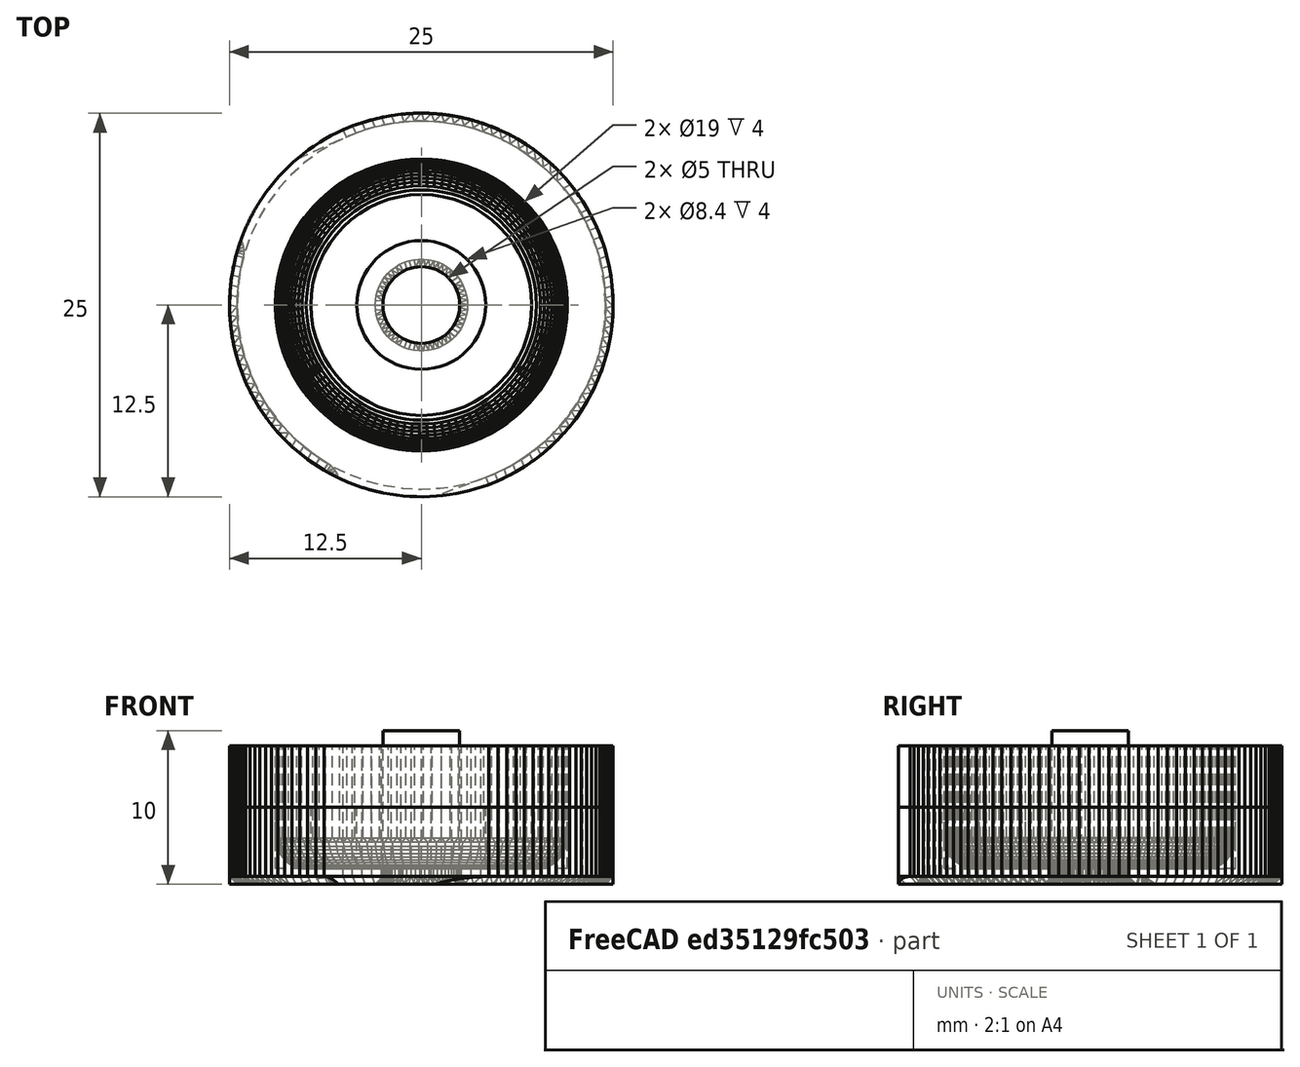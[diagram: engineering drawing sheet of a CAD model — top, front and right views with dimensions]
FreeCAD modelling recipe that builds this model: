
FCSTD DOCUMENT  (FreeCAD 0.18R14555 (Git shallow))
Label: bed-spring-holder
License: All rights reserved
LicenseURL: http://en.wikipedia.org/wiki/All_rights_reserved
objects: Part::Cylinder×9, Part::Cut×4, Part::Feature×3, Mesh::Feature×1, Part::MultiCommon×1, Part::MultiFuse×1, Part::Chamfer×1
note: 19 computed .brp shape members not serialized (recipe doc carries the construction recipe); baked Part::Feature solids carry a one-line shape summary decoded from their .brp

FEATURE [Mesh::Feature] CR_10_Y_Axis_wire_restrain_bracket  label="CR-10_Y-Axis_wire_restrain_bracket"
FEATURE [Part::Feature] CR_10_Y_Axis_wire_restrain_bracket001
  shape: bbox 76.5 x 39.68 x 21 mm, 5874 faces, 0 solids (baked)
FEATURE [Part::Feature] CR_10_Y_Axis_wire_restrain_bracket001_solid  label="CR_10_Y_Axis_wire_restrain_bracket001 (Solid)"
  shape: bbox 76.5 x 39.68 x 21 mm, 5874 faces (baked)
FEATURE [Part::Cylinder] Cylinder
  Angle = 360
  AttacherType = Attacher::AttachEngine3D
  Height = 10
  Radius = 12.5
FEATURE [Part::MultiCommon] Common
  Shapes = -> [Cylinder,CR_10_Y_Axis_wire_restrain_bracket001_solid]
FEATURE [Part::Cylinder] Cylinder001
  Angle = 360
  AttacherType = Attacher::AttachEngine3D
  Height = 10
  Radius = 4.2
FEATURE [Part::Cylinder] Cylinder002
  Angle = 360
  AttacherType = Attacher::AttachEngine3D
  Height = 10
  Radius = 7.2
FEATURE [Part::Cylinder] Cylinder003
  Angle = 360
  AttacherType = Attacher::AttachEngine3D
  Height = 10
  Radius = 2.5
FEATURE [Part::Cut] Cut
  Base = -> Cylinder002
  Tool = -> Cylinder001
FEATURE [Part::Cylinder] Cylinder004
  Angle = 360
  AttacherType = Attacher::AttachEngine3D
  Height = 10
  Radius = 12.5
FEATURE [Part::Cylinder] Cylinder005
  Angle = 360
  AttacherType = Attacher::AttachEngine3D
  Height = 10
  Radius = 9.5
FEATURE [Part::Cut] Cut001
  Base = -> Cylinder004
  Tool = -> Cylinder005
FEATURE [Part::Cylinder] Cylinder006
  Angle = 360
  AttacherType = Attacher::AttachEngine3D
  Height = 1
  Radius = 12.5
FEATURE [Part::MultiFuse] Fusion
  Shapes = -> [Cylinder006,Cut001,Cut]
FEATURE [Part::Cylinder] Cylinder007
  Angle = 360
  AttacherType = Attacher::AttachEngine3D
  Height = 10
  Radius = 2.5
FEATURE [Part::Cut] Cut002
  Base = -> Fusion
  Tool = -> Cylinder007
FEATURE [Part::Cylinder] Cylinder008
  Angle = 360
  AttacherType = Attacher::AttachEngine3D
  Height = 10
  Placement = pos=(0,0,5) rot=(0,0,1;0rad)
  Radius = 12.5
FEATURE [Part::Cut] Cut003
  Base = -> Cut002
  Tool = -> Cylinder008
FEATURE [Part::Feature] Cut003001  label="Cut004"
  shape: bbox 25 x 25 x 5 mm, 10 faces (baked)
FEATURE [Part::Chamfer] Chamfer
  Base = -> Cut003001
  Edges = 1 edges r=0.5: [Edge14]
